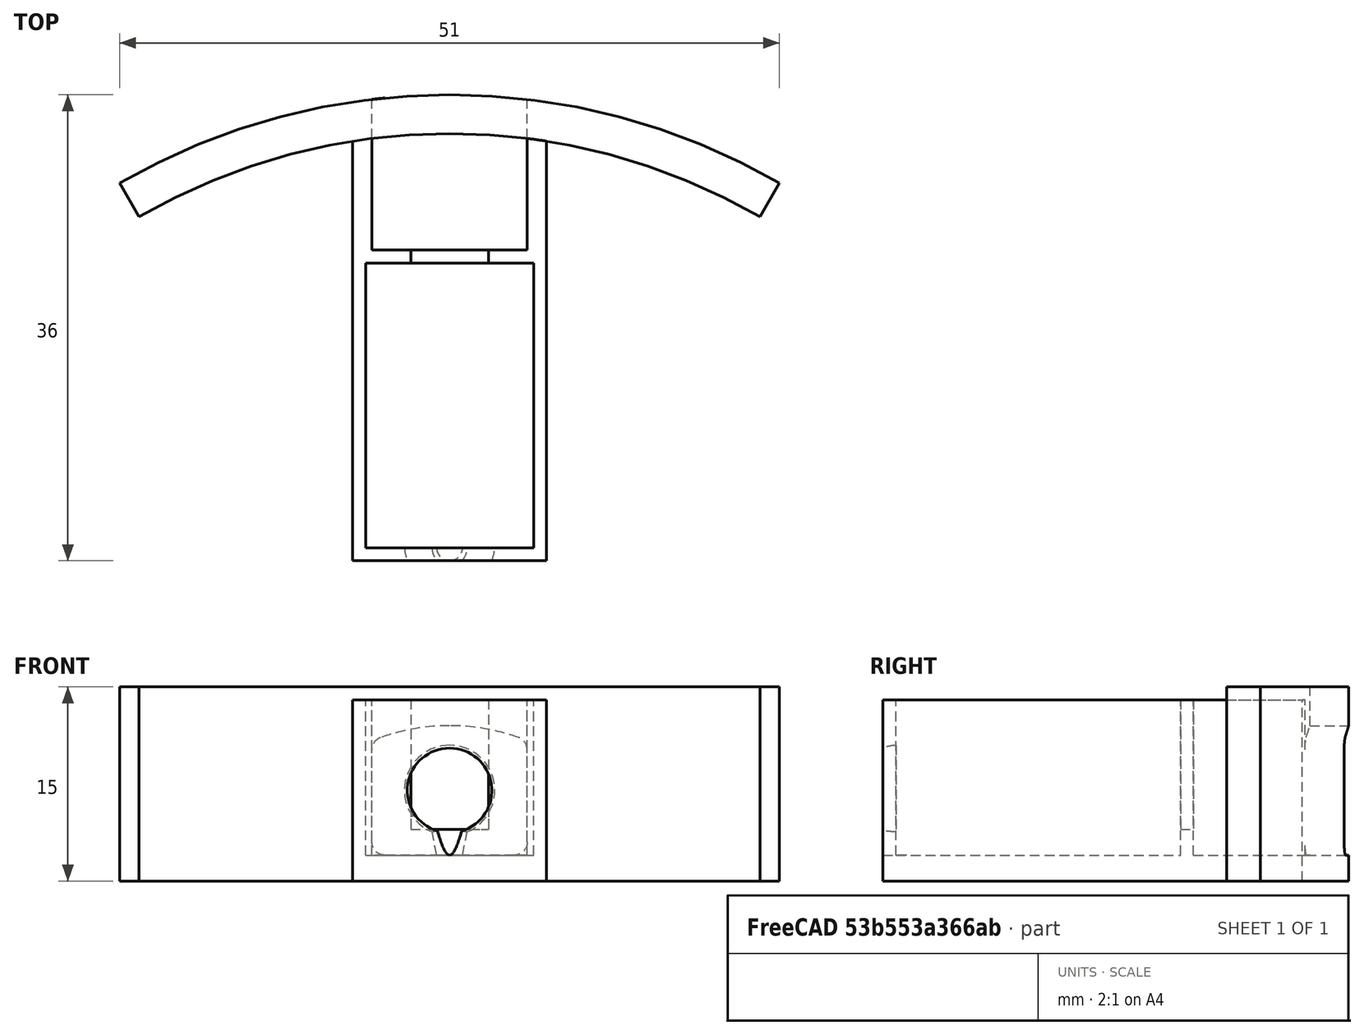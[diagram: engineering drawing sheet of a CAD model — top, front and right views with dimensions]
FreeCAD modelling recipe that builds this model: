
FCSTD DOCUMENT  (FreeCAD 0.16R4924 (Git))
Label: solenoid_bay_and_wall_v2
License: All rights reserved
LicenseURL: http://en.wikipedia.org/wiki/All_rights_reserved
objects: Part::Cut×8, Part::Box×5, Part::Cylinder×2, Part::MultiFuse×2, Part::Feature×2, Part::Extrusion×2, Part::Sphere×1, Part::Cone×1, Part::Thickness×1
note: 24 computed .brp shape members not serialized (recipe doc carries the construction recipe); baked Part::Feature solids carry a one-line shape summary decoded from their .brp

FEATURE [Part::Box] Box  label="Case"
  Height = 14
  Length = 15
  Placement = pos=(1,6,0) rot=(0,0,1;0rad)
  Width = 34
FEATURE [Part::Box] Box001  label="solenoidBay"
  Height = 12
  Length = 13
  Placement = pos=(2,7,2) rot=(0,0,1;0rad)
  Width = 22
FEATURE [Part::Cut] Cut
  Base = -> Box
  Tool = -> Box001
FEATURE [Part::Box] Box002  label="pullBay"
  Height = 15
  Length = 12
  Placement = pos=(2.5,30,2) rot=(0,0,1;0rad)
  Width = 10
FEATURE [Part::Cut] Cut001
  Base = -> Cut
  Tool = -> Box002
FEATURE [Part::Box] Box003  label="neck"
  Height = 15
  Length = 6
  Placement = pos=(5.5,28,4) rot=(0,0,1;0rad)
  Width = 4
FEATURE [Part::Cut] Cut002
  Base = -> Cut001
  Tool = -> Box003
FEATURE [Part::Sphere] Sphere  label="pinhole"
  Angle1 = -90
  Angle2 = 90
  Angle3 = 360
  Placement = pos=(8.5,7.25,7) rot=(0,0,1;0rad)
  Radius = 3.5
FEATURE [Part::Cut] Cut003
  Base = -> Cut002
  Tool = -> Sphere
FEATURE [Part::Cone] Cone
  Angle = 360
  Height = 5
  Placement = pos=(8.5,7,2) rot=(0,0,1;0rad)
  Radius1 = 1
  Radius2 = 2
FEATURE [Part::Cut] Cut004
  Base = -> Cut003
  Tool = -> Cone
FEATURE [Part::Cylinder] Cylinder  label="bottle_wall"
  Angle = 60
  Height = 15
  Placement = pos=(8.5,-7,0) rot=(0,0,1;1.0472rad)
  Radius = 51
FEATURE [Part::Cylinder] Cylinder001  label="bottle_wall001"
  Angle = 60
  Height = 15
  Placement = pos=(8.5,-7,0) rot=(0,0,1;1.0472rad)
  Radius = 48
FEATURE [Part::Cut] Cut005
  Base = -> Cylinder
  Placement = pos=(0,-2,0) rot=(0,0,1;0rad)
  Tool = -> Cylinder001
FEATURE [Part::MultiFuse] Fusion
  Shapes = -> [Cut004,Cut005]
FEATURE [Part::Box] Box004  label="pin_opening"
  Height = 5
  Length = 5
  Placement = pos=(6,38.5,5) rot=(0,0,1;0rad)
  Width = 5
FEATURE [Part::Cut] Cut006
  Base = -> Fusion
  Tool = -> Box004
FEATURE [Part::Feature] Common_cs  label="pin_cs"
  Placement = pos=(3.5,35,2) rot=(0,0,1;0rad)
  shape: bbox 10 x 2e-07 x 8 mm, 0 faces, 0 solids (baked)
FEATURE [Part::Extrusion] Extrude
  Base = -> Common_cs
  Dir = (0,5,0)
  Solid = true
FEATURE [Part::Thickness] Thickness
  Faces = -> Extrude [Face7]
  Intersection = false
  Join = 0
  Mode = 0
  SelfIntersection = false
  Value = 1
FEATURE [Part::Feature] Common_cs001  label="pin_cs001"
  Placement = pos=(3.5,35,2) rot=(0,0,1;0rad)
  shape: bbox 10 x 2e-07 x 8 mm, 0 faces, 0 solids (baked)
FEATURE [Part::Extrusion] Extrude001
  Base = -> Common_cs001
  Dir = (0,5,0)
  Solid = true
FEATURE [Part::MultiFuse] Fusion001
  Placement = pos=(0,-7,1) rot=(0,0,1;0rad)
  Shapes = -> [Thickness,Extrude,Extrude001]
FEATURE [Part::Cut] Cut007
  Base = -> Cut006
  Tool = -> Fusion001
